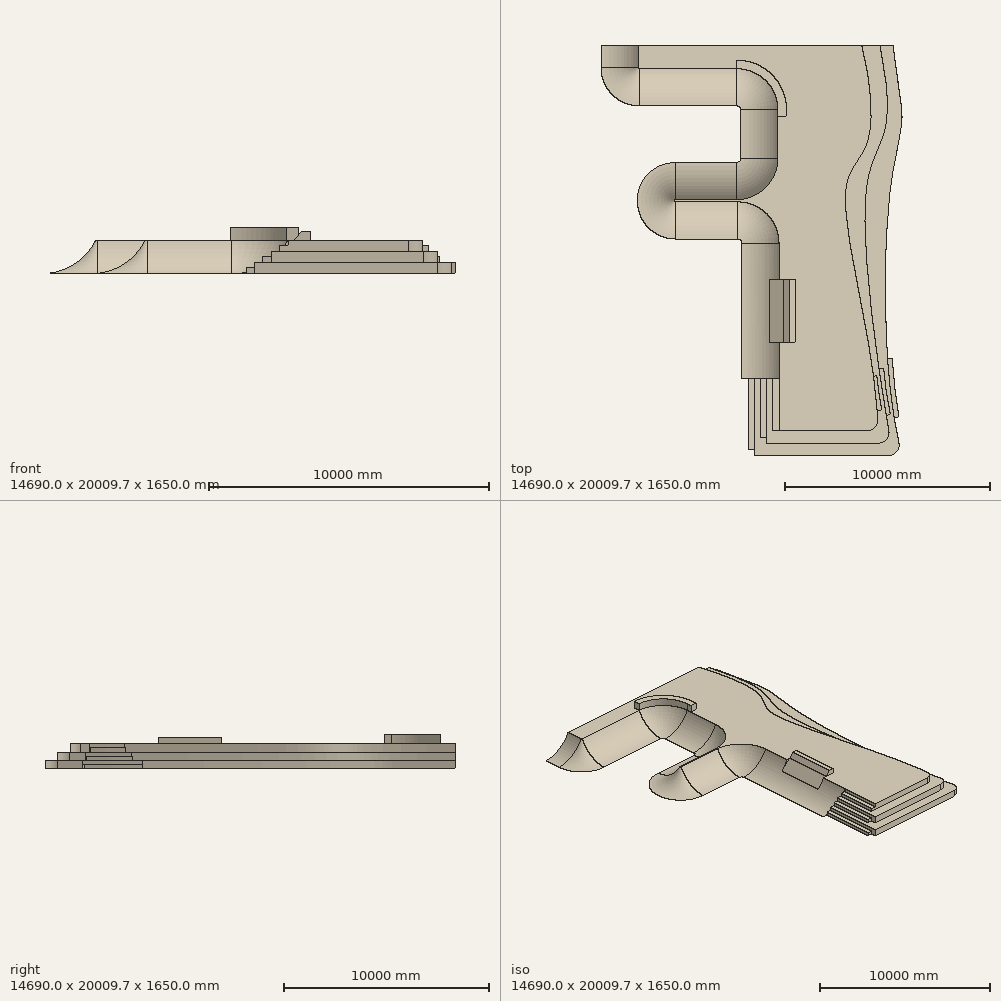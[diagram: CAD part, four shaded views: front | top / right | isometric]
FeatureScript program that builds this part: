
annotation { "Feature Type Name" : "Feature", "Feature Type Description" : "" }
export const myFeature = defineFeature(function(context is Context, id is Id, definition is map)
    precondition{}
    {
        {
            var Q0;
            Q0=qCreatedBy(makeId("Top.planeOp"),FACE);
            var sketch = newSketch(context, id + "F0", { "sketchPlane" : qUnion([Q0])});
            skLineSegment(sketch, "E0.bottom", {"start": v(-10000, 10000) * mm, "end": v(10000, 10000) * mm, "construction": true});
            skLineSegment(sketch, "E0.top", {"start": v(-10000, -10000) * mm, "end": v(10000, -10000) * mm, "construction": true});
            skLineSegment(sketch, "E0.left", {"start": v(-10000, 10000) * mm, "end": v(-10000, -10000) * mm, "construction": true});
            skLineSegment(sketch, "E0.right", {"start": v(10000, 10000) * mm, "end": v(10000, -10000) * mm, "construction": true});
            skPoint(sketch, "E0.middle", {"position": v(0, 0) * mm});
            skFitSpline(sketch, "E1", {"points": [v(9560.04, 10000) * mm, v(10000, 6463.48) * mm, v(9454.53, 3145.56) * mm, v(10000, -10009.66) * mm], "startDerivative": vector(2086.35, -20425.43) * mm, "endDerivative": vector(6192.41, -23586.92) * mm});
            skFitSpline(sketch, "E2", {"points": [v(8931.26, 10000) * mm, v(9144.55, 5788.3) * mm, v(8291.74, 3184.32) * mm, v(9461.17, -9409.66) * mm], "startDerivative": vector(3840.36, -19406.88) * mm, "endDerivative": vector(4228.66, -24367.98) * mm});
            skFitSpline(sketch, "E3", {"points": [v(8036.48, 10000) * mm, v(8280.1, 5181.32) * mm, v(7283.98, 3106.8) * mm, v(8828.62, -8809.66) * mm], "startDerivative": vector(4254.77, -16380.06) * mm, "endDerivative": vector(399.76, -26806.19) * mm});
            skLineSegment(sketch, "E4", {"start": v(9364.7, -10009.66) * mm, "end": v(2800, -10009.66) * mm});
            skLineSegment(sketch, "E5", {"start": v(8868.07, -9409.66) * mm, "end": v(3400, -9409.66) * mm});
            skLineSegment(sketch, "E6", {"start": v(8313.2, -8809.66) * mm, "end": v(4000, -8809.66) * mm});
            skArc(sketch, "E7.filletArc", {"start": v(8313.2, -8809.66) * mm, "mid": v(8674.67, -8655.12) * mm, "end": v(8812.7, -8287.04) * mm});
            skArc(sketch, "E8.filletArc", {"start": v(8868.07, -9409.66) * mm, "mid": v(9250.04, -9232.3) * mm, "end": v(9361.02, -8826.03) * mm});
            skArc(sketch, "E9.filletArc", {"start": v(9364.7, -10009.66) * mm, "mid": v(9754.8, -9822.41) * mm, "end": v(9852.74, -9400.93) * mm});
            skLineSegment(sketch, "E10", {"start": v(2800, -10009.66) * mm, "end": v(2800, -6262.37) * mm});
            skLineSegment(sketch, "E11", {"start": v(3400, -9409.66) * mm, "end": v(3400, -6262.37) * mm});
            skLineSegment(sketch, "E12", {"start": v(4000, -8809.66) * mm, "end": v(4000, 10000) * mm});
            skLineSegment(sketch, "E13", {"start": v(4000, 10000) * mm, "end": v(8036.48, 10000) * mm});
            skLineSegment(sketch, "E14", {"start": v(8931.26, 10000) * mm, "end": v(9560.04, 10000) * mm});
            skLineSegment(sketch, "E15", {"start": v(8931.26, 10000) * mm, "end": v(8036.48, 10000) * mm});
            skLineSegment(sketch, "E16", {"start": v(3400, -6262.37) * mm, "end": v(4000, -6262.37) * mm});
            skLineSegment(sketch, "E17", {"start": v(4000, -6262.37) * mm, "end": v(2800, -6262.37) * mm});
            skLineSegment(sketch, "E18", {"start": v(8812.7, 7275.7) * mm, "end": v(8812.7, -13881.84) * mm, "construction": true});
            skLineSegment(sketch, "E19", {"start": v(3700, -6262.37) * mm, "end": v(3700, -8809.66) * mm});
            skLineSegment(sketch, "E20", {"start": v(3700, -8809.66) * mm, "end": v(4000, -8809.66) * mm});
            skLineSegment(sketch, "E21", {"start": v(2800, -6262.37) * mm, "end": v(2500, -6262.37) * mm});
            skLineSegment(sketch, "E22", {"start": v(2500, -6262.37) * mm, "end": v(2500, -9709.66) * mm});
            skLineSegment(sketch, "E23", {"start": v(2500, -9709.66) * mm, "end": v(2800, -9709.66) * mm});
            skLineSegment(sketch, "E24", {"start": v(3100, -6262.37) * mm, "end": v(3100, -9109.66) * mm});
            skLineSegment(sketch, "E25", {"start": v(3100, -9109.66) * mm, "end": v(3400, -9109.66) * mm});
            skLineSegment(sketch, "E26", {"start": v(9619.93, -8184.04) * mm, "end": v(9853.32, -8129.6) * mm});
            skLineSegment(sketch, "E27", {"start": v(9519.51, -5254.77) * mm, "end": v(9288.82, -5281.55) * mm});
            skFitSpline(sketch, "E28", {"points": [v(9519.51, -5254.77) * mm, v(9650.48, -6715.09) * mm, v(9853.32, -8129.6) * mm], "startDerivative": vector(223.02, -2915.76) * mm, "endDerivative": vector(445.06, -2833.73) * mm});
            skLineSegment(sketch, "E29", {"start": v(9232.66, -8057.32) * mm, "end": v(9433.1, -8018.45) * mm});
            skLineSegment(sketch, "E30", {"start": v(8881.49, -5800.6) * mm, "end": v(9107.9, -5765.88) * mm});
            skFitSpline(sketch, "E31", {"points": [v(9107.9, -5765.88) * mm, v(9233.37, -6896.73) * mm, v(9433.1, -8018.45) * mm], "startDerivative": vector(213.97, -2267.44) * mm, "endDerivative": vector(436.42, -2237.71) * mm});
            skLineSegment(sketch, "E32", {"start": v(8613.23, -6148.29) * mm, "end": v(8765.39, -6118.99) * mm});
            skLineSegment(sketch, "E33", {"start": v(8787.84, -7848.29) * mm, "end": v(9020.3, -7803.19) * mm});
            skFitSpline(sketch, "E34", {"points": [v(8770.68, -6117.97) * mm, v(8902.5, -7155.19) * mm, v(9020.3, -7803.19) * mm], "startDerivative": vector(228.14, -1970.82) * mm, "endDerivative": vector(272.8, -1376.85) * mm});
            skArc(sketch, "E35.filletArc", {"start": v(8771.3, -6123.32) * mm, "mid": v(8769.3, -6119.86) * mm, "end": v(8765.39, -6118.99) * mm});
            skLineSegment(sketch, "E36", {"start": v(2240.3, -6262.37) * mm, "end": v(2240.3, 358.4) * mm});
            skLineSegment(sketch, "E37", {"start": v(1990.3, 608.4) * mm, "end": v(-1051.76, 608.4) * mm});
            skLineSegment(sketch, "E38", {"start": v(1938, 4232.4) * mm, "end": v(-1051.76, 4232.4) * mm});
            skArc(sketch, "E39", {"start": v(-1051.76, 4232.4) * mm, "mid": v(-2863.76, 2420.4) * mm, "end": v(-1051.76, 608.4) * mm});
            skLineSegment(sketch, "E40", {"start": v(2188, 4482.4) * mm, "end": v(2188, 6856.24) * mm});
            skLineSegment(sketch, "E41", {"start": v(1938, 7106.24) * mm, "end": v(-2824.02, 7106.24) * mm});
            skPoint(sketch, "E42.visualSharp", {"position": v(2188, 4232.4) * mm});
            skArc(sketch, "E42.filletArc", {"start": v(1938, 4232.4) * mm, "mid": v(2114.78, 4305.63) * mm, "end": v(2188, 4482.4) * mm});
            skPoint(sketch, "E43.visualSharp", {"position": v(2188, 7106.24) * mm});
            skArc(sketch, "E43.filletArc", {"start": v(2188, 6856.24) * mm, "mid": v(2114.78, 7033.02) * mm, "end": v(1938, 7106.24) * mm});
            skPoint(sketch, "E44.visualSharp", {"position": v(2240.3, 608.4) * mm});
            skArc(sketch, "E44.filletArc", {"start": v(2240.3, 358.4) * mm, "mid": v(2167.08, 535.18) * mm, "end": v(1990.3, 608.4) * mm});
            skArc(sketch, "E45", {"start": v(-2824.02, 7106.24) * mm, "mid": v(-4105.3, 7636.96) * mm, "end": v(-4636.02, 8918.24) * mm});
            skLineSegment(sketch, "E46", {"start": v(-4636.02, 8918.24) * mm, "end": v(-4636.02, 10000) * mm});
            skSolve(sketch);
        }
        {
            var Q0;
            Q0=makeQuery(id+"F0.imprint","IMPRINT",FACE,{"disambiguationData":[TD([[makeQuery(id+"F0.imprint","IMPRINT",EDGE,{"derivedFrom":sQuery(id+"F0.wireOp",EDGE,"E3")}),-1.0]])]});
            extrude(context, id + "F1", {"entities" : qUnion([Q0]), "depth" : 1200 * mm, "offsetDistance" : 25 * mm});
        }
        {
            var Q0;
            {var subQ4=sQuery(id+"F0.wireOp",EDGE,"E19");Q0=makeQuery(id+"F0.imprint","IMPRINT",FACE,{"disambiguationData":[TD([[makeQuery(id+"F0.imprint","IMPRINT",EDGE,{"derivedFrom":subQ4}),1.0]])]});}
            extrude(context, id + "F2", {"entities" : qUnion([Q0]), "operationType" : NewBodyOperationType.ADD, "depth" : 1000 * mm, "offsetDistance" : 25 * mm});
        }
        {
            var Q0;
            Q0=makeQuery(id+"F0.imprint","IMPRINT",FACE,{"disambiguationData":[TD([[makeQuery(id+"F0.imprint","IMPRINT",EDGE,{"derivedFrom":sQuery(id+"F0.wireOp",EDGE,"E2")}),-1.0]])]});
            var Q1;
            {var subQ4=sQuery(id+"F0.wireOp",EDGE,"E19");Q1=makeQuery(id+"F0.imprint","IMPRINT",FACE,{"disambiguationData":[TD([[makeQuery(id+"F0.imprint","IMPRINT",EDGE,{"derivedFrom":subQ4}),1.0]])]});}
            extrude(context, id + "F3", {"entities" : qUnion([Q0, Q1]), "operationType" : NewBodyOperationType.ADD, "depth" : 800 * mm, "offsetDistance" : 25 * mm});
        }
        {
            var Q0;
            Q0=makeQuery(id+"F0.imprint","IMPRINT",FACE,{"disambiguationData":[TD([[makeQuery(id+"F0.imprint","IMPRINT",EDGE,{"derivedFrom":sQuery(id+"F0.wireOp",EDGE,"E1")}),-1.0]])]});
            var Q1;
            {var subQ3=sQuery(id+"F0.wireOp",EDGE,"FLUqqUvB-q2nC-rusL-8V00-f9DvSJMesruP");Q1=makeQuery(id+"F0.imprint","IMPRINT",FACE,{"disambiguationData":[TD([[makeQuery(id+"F0.imprint","IMPRINT",EDGE,{"derivedFrom":subQ3}),-1.0]])]});}
            extrude(context, id + "F4", {"entities" : qUnion([Q0, Q1]), "operationType" : NewBodyOperationType.ADD, "depth" : 400 * mm, "offsetDistance" : 25 * mm});
        }
        {
            var Q0;
            {var subQ0=sQuery(id+"F0.wireOp",EDGE,"E21");Q0=makeQuery(id+"F0.imprint","IMPRINT",FACE,{"disambiguationData":[TD([[makeQuery(id+"F0.imprint","IMPRINT",EDGE,{"derivedFrom":subQ0}),1.0]])]});}
            extrude(context, id + "F5", {"entities" : qUnion([Q0]), "operationType" : NewBodyOperationType.ADD, "depth" : 200 * mm, "offsetDistance" : 25 * mm});
        }
        {
            var Q0;
            {var subQ4=sQuery(id+"F0.wireOp",EDGE,"E24");Q0=makeQuery(id+"F0.imprint","IMPRINT",FACE,{"disambiguationData":[TD([[makeQuery(id+"F0.imprint","IMPRINT",EDGE,{"derivedFrom":subQ4}),1.0]])]});}
            extrude(context, id + "F6", {"entities" : qUnion([Q0]), "operationType" : NewBodyOperationType.ADD, "depth" : 600 * mm, "offsetDistance" : 25 * mm});
        }
        {
            var Q0;
            {var subQ0=sQuery(id+"F0.wireOp",EDGE,"E26");Q0=makeQuery(id+"F0.imprint","IMPRINT",FACE,{"disambiguationData":[TD([[makeQuery(id+"F0.imprint","IMPRINT",EDGE,{"derivedFrom":subQ0}),1.0]])]});}
            extrude(context, id + "F7", {"entities" : qUnion([Q0]), "operationType" : NewBodyOperationType.ADD, "depth" : 200 * mm, "offsetDistance" : 25 * mm});
        }
        {
            var Q0;
            {var subQ0=sQuery(id+"F0.wireOp",EDGE,"E29");Q0=makeQuery(id+"F0.imprint","IMPRINT",FACE,{"disambiguationData":[TD([[makeQuery(id+"F0.imprint","IMPRINT",EDGE,{"derivedFrom":subQ0}),1.0]])]});}
            extrude(context, id + "F8", {"entities" : qUnion([Q0]), "operationType" : NewBodyOperationType.ADD, "depth" : 600 * mm, "offsetDistance" : 25 * mm});
        }
        {
            var Q0;
            {var subQ0=sQuery(id+"F0.wireOp",EDGE,"E32");Q0=makeQuery(id+"F0.imprint","IMPRINT",FACE,{"disambiguationData":[TD([[makeQuery(id+"F0.imprint","IMPRINT",EDGE,{"derivedFrom":subQ0}),-1.0]])]});}
            extrude(context, id + "F9", {"entities" : qUnion([Q0]), "operationType" : NewBodyOperationType.ADD, "depth" : 1000 * mm, "offsetDistance" : 25 * mm});
        }
        {
            var Q0;
            Q0=sQuery(id+"F0.wireOp",VERTEX,"E36.start");
            var Q1;
            Q1=sQuery(id+"F0.wireOp",EDGE,"E36");
            cPlane(context, id + "F10", {"entities" : qUnion([Q0, Q1]), "cplaneType" : CPlaneType.LINE_POINT, "offset" : 25 * mm, "width" : 150 * mm, "height" : 150 * mm});
        }
        {
            var Q0;
            Q0=qCreatedBy(id+"F10.planeOp",FACE);
            var sketch = newSketch(context, id + "F11", { "sketchPlane" : qUnion([Q0])});
            skLineSegment(sketch, "E47", {"start": v(-3937.31, 2133.6) * mm, "end": v(-894.14, 2133.6) * mm, "construction": true});
            skPoint(sketch, "E48.0", {"position": v(-4000, 1200) * mm});
            skArc(sketch, "E49", {"start": v(-4000, 1200) * mm, "mid": v(-3258.1, 351.8) * mm, "end": v(-2187.54, 0) * mm});
            skLineSegment(sketch, "E50.0", {"start": v(-4000, 1200) * mm, "end": v(-4000, 1000) * mm});
            skLineSegment(sketch, "E51", {"start": v(-2187.54, 0) * mm, "end": v(-4000, 0) * mm});
            skPoint(sketch, "E51.endSnap0", {"position": v(-4000, 1100) * mm});
            skLineSegment(sketch, "E52", {"start": v(-4000, 0) * mm, "end": v(-4000, 1200) * mm});
            skLineSegment(sketch, "E53", {"start": v(-4000, 1200) * mm, "end": v(-3877.24, 980.67) * mm, "construction": true});
            skLineSegment(sketch, "E54.0", {"start": v(-8313.2, 1200) * mm, "end": v(-4000, 1200) * mm});
            skSolve(sketch);
        }
        {
            var Q0;
            {var subQ0=sQuery(id+"F11.wireOp",EDGE,"E49");Q0=makeQuery(id+"F11.imprint","IMPRINT",FACE,{"disambiguationData":[TD([[makeQuery(id+"F11.imprint","IMPRINT",EDGE,{"derivedFrom":subQ0}),-1.0]])]});}
            var Q1;
            Q1=sQuery(id+"F11.wireOp",EDGE,"E49");
            var Q2;
            Q2=sQuery(id+"F0.wireOp",EDGE,"E41");
            var Q3;
            Q3=sQuery(id+"F0.wireOp",EDGE,"E43.filletArc");
            var Q4;
            Q4=sQuery(id+"F0.wireOp",EDGE,"E40");
            var Q5;
            Q5=sQuery(id+"F0.wireOp",EDGE,"E42.filletArc");
            var Q6;
            Q6=sQuery(id+"F0.wireOp",EDGE,"E38");
            var Q7;
            Q7=sQuery(id+"F0.wireOp",EDGE,"E39");
            var Q8;
            Q8=sQuery(id+"F0.wireOp",EDGE,"E37");
            var Q9;
            Q9=sQuery(id+"F0.wireOp",EDGE,"E44.filletArc");
            var Q10;
            Q10=sQuery(id+"F0.wireOp",EDGE,"E36");
            var Q11;
            Q11=sQuery(id+"F0.wireOp",EDGE,"E45");
            var Q12;
            Q12=sQuery(id+"F0.wireOp",EDGE,"E46");
            sweep(context, id + "F12", {"operationType" : NewBodyOperationType.ADD, "profiles" : qUnion([Q0]), "surfaceProfiles" : qUnion([Q1]), "path" : qUnion([Q2, Q3, Q4, Q5, Q6, Q7, Q8, Q9, Q10, Q11, Q12])});
        }
        {
            var Q0;
            Q0=makeQuery(id+"F12.boolean.opBoolean","MERGE",EDGE,{"derivedFrom":[makeQuery(id+"F1.opExtrude","CAP_EDGE",EDGE,{"disambiguationData":[OSD([sQuery(id+"F0.wireOp",EDGE,"E12")])],"isStart":false}),makeQuery(id+"F12.opSweep","SWEPT_EDGE",EDGE,{"disambiguationData":[OSD([sQuery(id+"F0.wireOp",EDGE,"E36"),sQuery(id+"F11.wireOp",EDGE,"E49"),sQuery(id+"F11.wireOp",EDGE,"E52")])]})]});
            cPoint(context, id + "F13", {"entities" : qUnion([Q0]), "parameter" : 0.5});
        }
        {
            var Q0;
            Q0 = qCreatedBy(id + "F13" ,VERTEX);
            var Q1;
            Q1=makeQuery(id+"F12.boolean.opBoolean","MERGE",EDGE,{"derivedFrom":[makeQuery(id+"F1.opExtrude","CAP_EDGE",EDGE,{"disambiguationData":[OSD([sQuery(id+"F0.wireOp",EDGE,"E12")])],"isStart":false}),makeQuery(id+"F12.opSweep","SWEPT_EDGE",EDGE,{"disambiguationData":[OSD([sQuery(id+"F0.wireOp",EDGE,"E36"),sQuery(id+"F11.wireOp",EDGE,"E49"),sQuery(id+"F11.wireOp",EDGE,"E52")])]})]});
            cPlane(context, id + "F14", {"entities" : qUnion([Q0, Q1]), "cplaneType" : CPlaneType.LINE_POINT, "offset" : 25 * mm, "width" : 150 * mm, "height" : 150 * mm});
        }
        {
            var Q0;
            Q0=qCreatedBy(id+"F14.planeOp",FACE);
            var sketch = newSketch(context, id + "F15", { "sketchPlane" : qUnion([Q0])});
            skLineSegment(sketch, "E55", {"start": v(-4500.62, 1500) * mm, "end": v(-4805.42, 1500) * mm});
            skLineSegment(sketch, "E56", {"start": v(-4805.42, 1500) * mm, "end": v(-4805.42, 1200) * mm});
            skLineSegment(sketch, "E57", {"start": v(-4805.42, 1200) * mm, "end": v(-4225.57, 1200) * mm});
            skLineSegment(sketch, "E58", {"start": v(-4225.57, 1200) * mm, "end": v(-3236.7, 1854.65) * mm});
            skLineSegment(sketch, "E59", {"start": v(-3236.7, 1854.65) * mm, "end": v(-1603.27, 735.4) * mm});
            skLineSegment(sketch, "E60", {"start": v(-1603.27, 735.4) * mm, "end": v(-3485.6, 525.55) * mm});
            skLineSegment(sketch, "E61", {"start": v(-3485.6, 525.55) * mm, "end": v(-4225.57, 1200) * mm});
            skLineSegment(sketch, "E62", {"start": v(-4500.62, 1500) * mm, "end": v(-4225.57, 1200) * mm});
            skLineSegment(sketch, "E63.0", {"start": v(-4000, 1200) * mm, "end": v(-8036.48, 1200) * mm});
            skSolve(sketch);
        }
        {
            var Q0;
            Q0=makeQuery(id+"F15.imprint","IMPRINT",FACE,{"disambiguationData":[TD([[makeQuery(id+"F15.imprint","IMPRINT",EDGE,{"derivedFrom":sQuery(id+"F15.wireOp",EDGE,"E55")}),1.0]])]});
            extrude(context, id + "F16", {"entities" : qUnion([Q0]), "operationType" : NewBodyOperationType.ADD, "depth" : 3048 * mm, "offsetDistance" : 25 * mm, "symmetric" : true});
        }
        {
            var Q0;
            Q0=makeQuery(id+"F15.imprint","IMPRINT",FACE,{"disambiguationData":[TD([[makeQuery(id+"F15.imprint","IMPRINT",EDGE,{"derivedFrom":sQuery(id+"F15.wireOp",EDGE,"E58")}),-1.0]])]});
            extrude(context, id + "F17", {"entities" : qUnion([Q0]), "operationType" : NewBodyOperationType.REMOVE, "oppositeDirection" : true, "depth" : 3048 * mm, "offsetDistance" : 25 * mm, "symmetric" : true});
        }
        {
            var Q0;
            {var subQ0=sQuery(id+"F0.wireOp",EDGE,"E35.filletArc");var subQ1=sQuery(id+"F0.wireOp",EDGE,"E34");var subQ2=sQuery(id+"F0.wireOp",EDGE,"E33");var subQ3=sQuery(id+"F0.wireOp",EDGE,"E32");var subQ4=sQuery(id+"F0.wireOp",EDGE,"E3");var subQ5=sQuery(id+"F0.wireOp",EDGE,"E31");var subQ6=sQuery(id+"F0.wireOp",EDGE,"E30");var subQ7=sQuery(id+"F0.wireOp",EDGE,"E29");var subQ8=sQuery(id+"F0.wireOp",EDGE,"E2");var subQ9=sQuery(id+"F0.wireOp",EDGE,"E1");var subQ10=sQuery(id+"F0.wireOp",EDGE,"E25");var subQ11=sQuery(id+"F0.wireOp",EDGE,"E24");var subQ12=sQuery(id+"F0.wireOp",EDGE,"E17");var subQ13=sQuery(id+"F0.wireOp",EDGE,"E11");var subQ14=sQuery(id+"F0.wireOp",EDGE,"E10");var subQ15=sQuery(id+"F0.wireOp",EDGE,"E8.filletArc");var subQ16=sQuery(id+"F0.wireOp",EDGE,"E5");var subQ17=sQuery(id+"F0.wireOp",EDGE,"E12");var subQ18=sQuery(id+"F0.wireOp",EDGE,"E7.filletArc");var subQ19=sQuery(id+"F0.wireOp",EDGE,"E6");Q0=makeQuery(id+"F12.boolean.opBoolean","MERGE",FACE,{"derivedFrom":[makeQuery(id+"F9.boolean.opBoolean","MERGE",FACE,{"derivedFrom":[makeQuery(id+"F8.boolean.opBoolean","MERGE",FACE,{"derivedFrom":[makeQuery(id+"F7.boolean.opBoolean","MERGE",FACE,{"derivedFrom":[makeQuery(id+"F6.boolean.opBoolean","MERGE",FACE,{"derivedFrom":[makeQuery(id+"F5.boolean.opBoolean","MERGE",FACE,{"derivedFrom":[makeQuery(id+"F4.boolean.opBoolean","MERGE",FACE,{"derivedFrom":[makeQuery(id+"F3.boolean.opBoolean","MERGE",FACE,{"derivedFrom":[makeQuery(id+"F2.boolean.opBoolean","MERGE",FACE,{"derivedFrom":[makeQuery(id+"F1.opExtrude","CAP_FACE",FACE,{"disambiguationData":[OSD([subQ4,subQ19,subQ18,subQ17,sQuery(id+"F0.wireOp",EDGE,"E13")])],"isStart":true}),makeQuery(id+"F2.opExtrude","CAP_FACE",FACE,{"disambiguationData":[OSD([subQ17,subQ12,sQuery(id+"F0.wireOp",EDGE,"E19"),sQuery(id+"F0.wireOp",EDGE,"E20")])],"isStart":true})]}),makeQuery(id+"F3.opExtrude","CAP_FACE",FACE,{"disambiguationData":[OSD([subQ8,subQ4,subQ16,subQ19,subQ18,subQ15,subQ13,subQ17,sQuery(id+"F0.wireOp",EDGE,"E15"),subQ12,subQ3,subQ2,subQ1,subQ0])],"isStart":true})]}),makeQuery(id+"F4.opExtrude","CAP_FACE",FACE,{"disambiguationData":[OSD([subQ9,subQ8,sQuery(id+"F0.wireOp",EDGE,"E4"),subQ16,subQ15,sQuery(id+"F0.wireOp",EDGE,"E9.filletArc"),subQ14,subQ13,sQuery(id+"F0.wireOp",EDGE,"E14"),subQ12,subQ11,subQ10,subQ7,subQ6,subQ5])],"isStart":true})]}),makeQuery(id+"F5.opExtrude","CAP_FACE",FACE,{"disambiguationData":[OSD([subQ14,sQuery(id+"F0.wireOp",EDGE,"E21"),sQuery(id+"F0.wireOp",EDGE,"E22"),sQuery(id+"F0.wireOp",EDGE,"E23")])],"isStart":true})]}),makeQuery(id+"F6.opExtrude","CAP_FACE",FACE,{"disambiguationData":[OSD([subQ13,subQ12,subQ11,subQ10])],"isStart":true})]}),makeQuery(id+"F7.opExtrude","CAP_FACE",FACE,{"disambiguationData":[OSD([subQ9,sQuery(id+"F0.wireOp",EDGE,"E26"),sQuery(id+"F0.wireOp",EDGE,"E27"),sQuery(id+"F0.wireOp",EDGE,"E28")])],"isStart":true})]}),makeQuery(id+"F8.opExtrude","CAP_FACE",FACE,{"disambiguationData":[OSD([subQ8,subQ7,subQ6,subQ5])],"isStart":true})]}),makeQuery(id+"F9.opExtrude","CAP_FACE",FACE,{"disambiguationData":[OSD([subQ4,subQ3,subQ2,subQ1,subQ0])],"isStart":true})]}),makeQuery(id+"F12.opSweep","SWEPT_FACE",FACE,{"disambiguationData":[OSD([sQuery(id+"F0.wireOp",EDGE,"E36"),sQuery(id+"F11.wireOp",EDGE,"E51")])]})]});}
            var sketch = newSketch(context, id + "F18", { "sketchPlane" : qUnion([Q0])});
            skLineSegment(sketch, "E64", {"start": v(4000, -10000) * mm, "end": v(-2876.33, -10000) * mm});
            skLineSegment(sketch, "E65", {"start": v(-2876.33, -10000) * mm, "end": v(-2876.33, -10000) * mm});
            skSolve(sketch);
        }
        {
            var Q0;
            Q0=makeQuery(id+"F18.imprint","IMPRINT",FACE,{"disambiguationData":[TD([[makeQuery(id+"F18.imprint","IMPRINT",EDGE,{"derivedFrom":sQuery(id+"F18.wireOp",EDGE,"E64")}),-1.0]])]});
            extrude(context, id + "F19", {"entities" : qUnion([Q0]), "operationType" : NewBodyOperationType.ADD, "oppositeDirection" : true, "depth" : 1200 * mm, "offsetDistance" : 25 * mm});
        }
        {
            var Q0;
            {var subQ0=sQuery(id+"F0.wireOp",EDGE,"E12");Q0=makeQuery(id+"F19.boolean.opBoolean","MERGE",FACE,{"derivedFrom":[makeQuery(id+"F1.opExtrude","CAP_FACE",FACE,{"disambiguationData":[OSD([sQuery(id+"F0.wireOp",EDGE,"E3"),sQuery(id+"F0.wireOp",EDGE,"E6"),sQuery(id+"F0.wireOp",EDGE,"E7.filletArc"),subQ0,sQuery(id+"F0.wireOp",EDGE,"E13")])],"isStart":false}),makeQuery(id+"F19.opExtrude","CAP_FACE",FACE,{"disambiguationData":[OSD([subQ0,sQuery(id+"F0.wireOp",EDGE,"E37"),sQuery(id+"F0.wireOp",EDGE,"E38"),sQuery(id+"F0.wireOp",EDGE,"E39"),sQuery(id+"F0.wireOp",EDGE,"E40"),sQuery(id+"F0.wireOp",EDGE,"E41"),sQuery(id+"F0.wireOp",EDGE,"E42.filletArc"),sQuery(id+"F0.wireOp",EDGE,"E43.filletArc"),sQuery(id+"F0.wireOp",EDGE,"E44.filletArc"),sQuery(id+"F11.wireOp",EDGE,"E51"),sQuery(id+"F11.wireOp",EDGE,"E52"),sQuery(id+"F18.wireOp",EDGE,"E64"),sQuery(id+"F18.wireOp",EDGE,"E65")])],"isStart":false})]});}
            var sketch = newSketch(context, id + "F20", { "sketchPlane" : qUnion([Q0])});
            skArc(sketch, "E66.0", {"start": v(3947.7, 6856.24) * mm, "mid": v(3359.07, 8277.3) * mm, "end": v(1938, 8865.94) * mm});
            skArc(sketch, "E67.0", {"start": v(4367.7, 6856.24) * mm, "mid": v(3656.05, 8574.3) * mm, "end": v(1938, 9285.94) * mm});
            skLineSegment(sketch, "E68", {"start": v(1938, 8865.94) * mm, "end": v(1938, 9285.94) * mm});
            skLineSegment(sketch, "E69", {"start": v(3947.7, 6856.24) * mm, "end": v(3947.7, 6544.58) * mm});
            skLineSegment(sketch, "E70", {"start": v(3947.7, 6544.58) * mm, "end": v(4367.7, 6544.58) * mm});
            skLineSegment(sketch, "E71", {"start": v(4367.7, 6544.58) * mm, "end": v(4367.7, 6856.24) * mm});
            skSolve(sketch);
        }
        {
            var Q0;
            Q0=makeQuery(id+"F20.imprint","IMPRINT",FACE,{"disambiguationData":[TD([[makeQuery(id+"F20.imprint","IMPRINT",EDGE,{"derivedFrom":sQuery(id+"F20.wireOp",EDGE,"E66.0")}),-1.0]])]});
            extrude(context, id + "F21", {"entities" : qUnion([Q0]), "operationType" : NewBodyOperationType.ADD, "depth" : 450 * mm, "offsetDistance" : 25 * mm});
        }
    });
